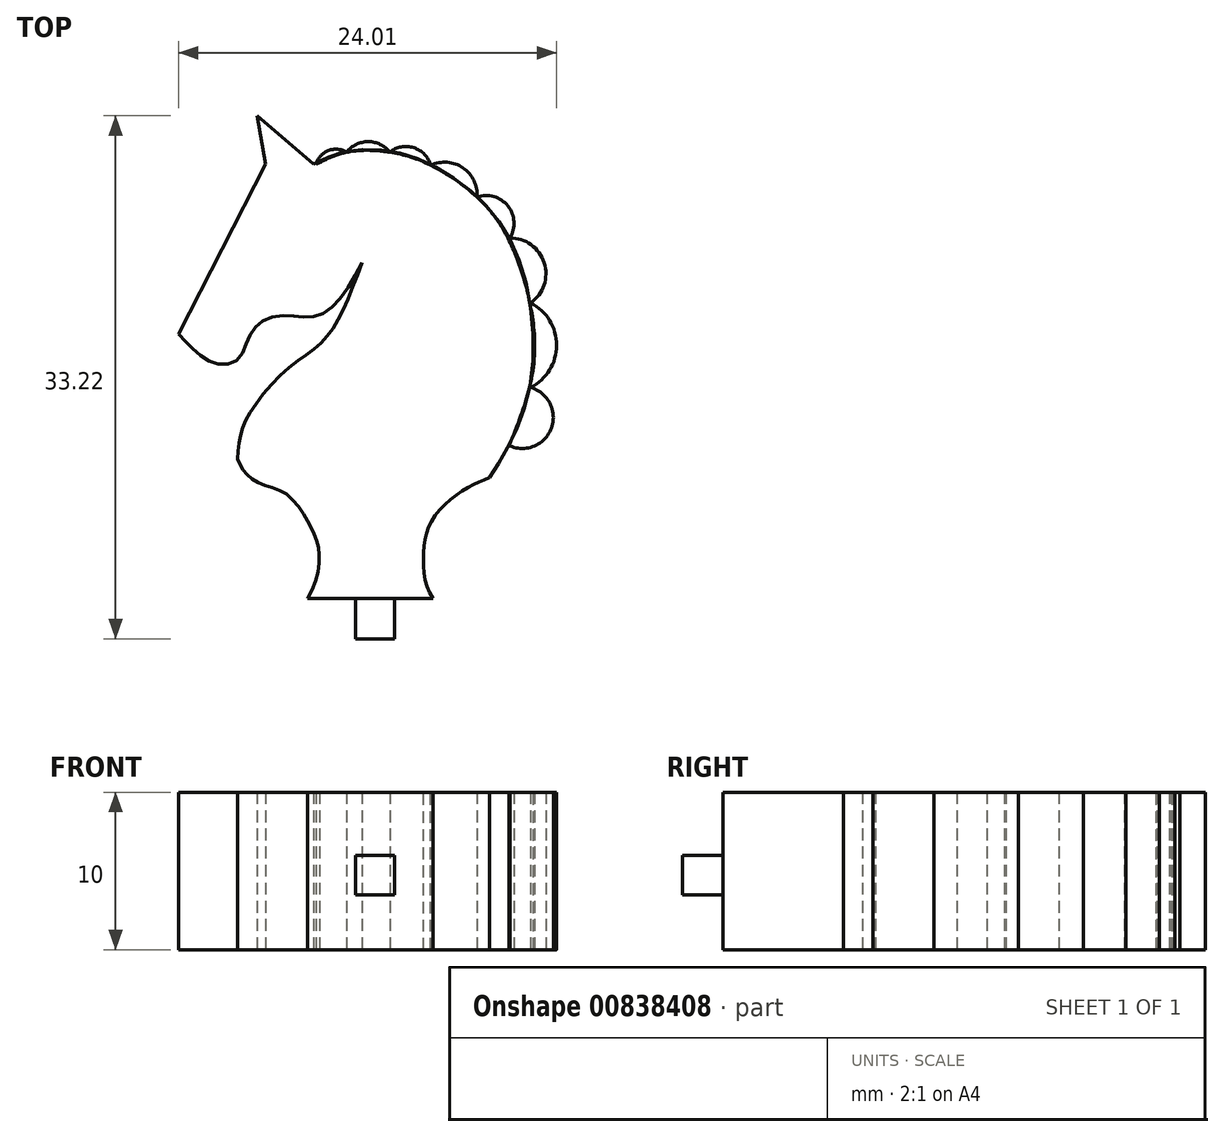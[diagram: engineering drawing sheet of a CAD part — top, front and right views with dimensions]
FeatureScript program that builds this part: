
annotation { "Feature Type Name" : "Feature", "Feature Type Description" : "" }
export const myFeature = defineFeature(function(context is Context, id is Id, definition is map)
    precondition{}
    {
        {
            var Q0;
            Q0=qCreatedBy(makeId("Top.planeOp"),FACE);
            var sketch = newSketch(context, id + "F0", { "sketchPlane" : qUnion([Q0])});
            skLineSegment(sketch, "E0", {"start": v(-12.48, 16.9) * mm, "end": v(-6.96, 27.69) * mm});
            skLineSegment(sketch, "E1", {"start": v(-6.96, 27.69) * mm, "end": v(-7.5, 30.77) * mm});
            skLineSegment(sketch, "E2", {"start": v(-7.5, 30.77) * mm, "end": v(-3.91, 27.69) * mm});
            skFitSpline(sketch, "E3", {"points": [v(-3.91, 27.69) * mm, v(-1.87, 28.5) * mm, v(0.86, 28.54) * mm, v(3.5, 27.69) * mm, v(6.44, 25.66) * mm, v(8.5, 23.04) * mm, v(9.85, 18.85) * mm, v(9.81, 13.52) * mm, v(8.53, 9.9) * mm, v(7.26, 7.78) * mm], "startDerivative": vector(21.4, 10.83) * mm, "endDerivative": vector(-13.49, -20.71) * mm});
            skFitSpline(sketch, "E4", {"points": [v(7.26, 7.78) * mm, v(5.6, 7) * mm, v(3.66, 5.15) * mm, v(3.09, 3.13) * mm, v(3.34, 0.79) * mm, v(4.65, -1.02) * mm, v(6.14, -1.95) * mm, v(7.6, -2.36) * mm], "startDerivative": vector(-11.83, -4.62) * mm, "endDerivative": vector(12.03, -2.67) * mm});
            skFitSpline(sketch, "E5", {"points": [v(-12.48, 16.9) * mm, v(-11.34, 15.75) * mm, v(-10, 15) * mm, v(-8.68, 15.33) * mm, v(-8.05, 16.63) * mm, v(-7.17, 17.71) * mm, v(-5.51, 18.09) * mm, v(-3.91, 18.01) * mm, v(-2.43, 18.92) * mm, v(-0.82, 21.45) * mm], "startDerivative": vector(10.15, -10.82) * mm, "endDerivative": vector(10.23, 19.07) * mm});
            skFitSpline(sketch, "E6", {"points": [v(-0.82, 21.45) * mm, v(-2.27, 17.96) * mm, v(-3.6, 16.18) * mm, v(-5.61, 14.65) * mm, v(-7.9, 11.99) * mm, v(-8.55, 10.48) * mm, v(-8.73, 8.97) * mm], "startDerivative": vector(-6.89, -18.3) * mm, "endDerivative": vector(-0.81, -11.84) * mm});
            skFitSpline(sketch, "E7", {"points": [v(-8.73, 8.97) * mm, v(-8.23, 8.08) * mm, v(-7.19, 7.37) * mm, v(-5.68, 6.77) * mm, v(-4.38, 5.2) * mm, v(-3.75, 3.89) * mm, v(-3.54, 2.38) * mm, v(-4.28, 0.1) * mm, v(-5.52, -1.32) * mm, v(-6.69, -2.04) * mm, v(-8.3, -2.4) * mm], "startDerivative": vector(5.04, -11.7) * mm, "endDerivative": vector(-16.8, -2.54) * mm});
            skLineSegment(sketch, "E8", {"start": v(-4.28, 0.1) * mm, "end": v(3.68, 0.1) * mm});
            skLineSegment(sketch, "E9", {"start": v(3.68, 0.1) * mm, "end": v(1.16, 0.1) * mm});
            skLineSegment(sketch, "E10", {"start": v(-4.28, 0.1) * mm, "end": v(-1.8, 0.1) * mm});
            skPoint(sketch, "E11.end.orphan", {"position": v(1.16, -4.9) * mm});
            skPoint(sketch, "E11.start.orphan", {"position": v(-1.8, -4.9) * mm});
            skSolve(sketch);
        }
        {
            var Q0;
            Q0=qCreatedBy(makeId("Top.planeOp"),FACE);
            var sketch = newSketch(context, id + "F1", { "sketchPlane" : qUnion([Q0])});
            skArc(sketch, "E12", {"start": v(-1.8, 28.46) * mm, "mid": v(-2.98, 28.56) * mm, "end": v(-3.76, 27.68) * mm});
            skArc(sketch, "E13", {"start": v(0.94, 28.46) * mm, "mid": v(-0.43, 29.13) * mm, "end": v(-1.8, 28.46) * mm});
            skArc(sketch, "E14", {"start": v(3.53, 27.63) * mm, "mid": v(2.46, 28.74) * mm, "end": v(0.94, 28.46) * mm});
            skArc(sketch, "E15", {"start": v(6.48, 25.6) * mm, "mid": v(5.59, 27.46) * mm, "end": v(3.53, 27.63) * mm});
            skArc(sketch, "E16", {"start": v(8.56, 23.01) * mm, "mid": v(8.44, 25.05) * mm, "end": v(6.48, 25.6) * mm});
            skArc(sketch, "E17", {"start": v(9.89, 18.88) * mm, "mid": v(10.74, 21.44) * mm, "end": v(8.56, 23.01) * mm});
            skArc(sketch, "E18", {"start": v(9.89, 13.51) * mm, "mid": v(11.53, 16.2) * mm, "end": v(9.89, 18.88) * mm});
            skArc(sketch, "E19", {"start": v(8.56, 9.8) * mm, "mid": v(11.2, 10.94) * mm, "end": v(9.89, 13.51) * mm});
            skLineSegment(sketch, "E20", {"start": v(9.89, 13.51) * mm, "end": v(9.81, 13.53) * mm});
            skLineSegment(sketch, "E21", {"start": v(9.89, 18.88) * mm, "end": v(9.83, 18.88) * mm});
            skLineSegment(sketch, "E22", {"start": v(8.56, 23.01) * mm, "end": v(8.43, 23.01) * mm});
            skLineSegment(sketch, "E23", {"start": v(-1.8, 28.46) * mm, "end": v(-1.8, 28.46) * mm});
            skFitSpline(sketch, "E24", {"points": [v(-3.76, 27.68) * mm, v(-1.8, 28.46) * mm, v(0.94, 28.46) * mm, v(3.53, 27.63) * mm, v(6.48, 25.6) * mm, v(8.43, 23.01) * mm, v(9.83, 18.88) * mm, v(9.81, 13.53) * mm, v(8.5, 9.8) * mm, v(8.5, 9.8) * mm], "startDerivative": vector(18.81, 9.57) * mm, "endDerivative": vector(0.25, 0.1) * mm});
            skLineSegment(sketch, "E25", {"start": v(8.56, 9.8) * mm, "end": v(8.5, 9.8) * mm});
            skSolve(sketch);
        }
        {
            var Q0;
            Q0=makeQuery(id+"F1.imprint","IMPRINT",FACE,{"disambiguationData":[TD([[makeQuery(id+"F1.imprint","IMPRINT",EDGE,{"derivedFrom":sQuery(id+"F1.wireOp",EDGE,"E17")}),1.0]])]});
            var Q1;
            Q1=makeQuery(id+"F1.imprint","IMPRINT",FACE,{"disambiguationData":[TD([[makeQuery(id+"F1.imprint","IMPRINT",EDGE,{"derivedFrom":sQuery(id+"F1.wireOp",EDGE,"E18")}),1.0]])]});
            var Q2;
            Q2=makeQuery(id+"F1.imprint","IMPRINT",FACE,{"disambiguationData":[TD([[makeQuery(id+"F1.imprint","IMPRINT",EDGE,{"derivedFrom":sQuery(id+"F1.wireOp",EDGE,"E19")}),1.0]])]});
            var Q3;
            {var subQ0=sQuery(id+"F1.wireOp",EDGE,"E16");Q3=makeQuery(id+"F1.imprint","IMPRINT",FACE,{"disambiguationData":[TD([[makeQuery(id+"F1.imprint","IMPRINT",EDGE,{"derivedFrom":subQ0}),1.0]])]});}
            var Q4;
            {var subQ0=sQuery(id+"F1.wireOp",EDGE,"E15");Q4=makeQuery(id+"F1.imprint","IMPRINT",FACE,{"disambiguationData":[TD([[makeQuery(id+"F1.imprint","IMPRINT",EDGE,{"derivedFrom":subQ0}),1.0]])]});}
            var Q5;
            {var subQ0=sQuery(id+"F1.wireOp",EDGE,"E14");Q5=makeQuery(id+"F1.imprint","IMPRINT",FACE,{"disambiguationData":[TD([[makeQuery(id+"F1.imprint","IMPRINT",EDGE,{"derivedFrom":subQ0}),1.0]])]});}
            var Q6;
            {var subQ0=sQuery(id+"F1.wireOp",EDGE,"E13");Q6=makeQuery(id+"F1.imprint","IMPRINT",FACE,{"disambiguationData":[TD([[makeQuery(id+"F1.imprint","IMPRINT",EDGE,{"derivedFrom":subQ0}),1.0]])]});}
            var Q7;
            {var subQ0=sQuery(id+"F1.wireOp",EDGE,"E12");Q7=makeQuery(id+"F1.imprint","IMPRINT",FACE,{"disambiguationData":[TD([[makeQuery(id+"F1.imprint","IMPRINT",EDGE,{"derivedFrom":subQ0}),1.0]])]});}
            extrude(context, id + "F2", {"entities" : qUnion([Q0, Q1, Q2, Q3, Q4, Q5, Q6, Q7]), "depth" : 10 * mm, "offsetDistance" : 25 * mm});
        }
        {
            var Q0;
            Q0=makeQuery(id+"F0.imprint","IMPRINT",FACE,{"disambiguationData":[TD([[makeQuery(id+"F0.imprint","IMPRINT",EDGE,{"derivedFrom":sQuery(id+"F0.wireOp",EDGE,"E0")}),-1.0]])]});
            extrude(context, id + "F3", {"entities" : qUnion([Q0]), "depth" : 10 * mm, "offsetDistance" : 25 * mm});
        }
        {
            var Q0;
            Q0=makeQuery(id+"F3.opExtrude","SWEPT_FACE",FACE,{"disambiguationData":[OSD([sQuery(id+"F0.wireOp",EDGE,"E8"),sQuery(id+"F0.wireOp",EDGE,"E9"),sQuery(id+"F0.wireOp",EDGE,"E10")])]});
            var sketch = newSketch(context, id + "F4", { "sketchPlane" : qUnion([Q0])});
            skSolve(sketch);
        }
        {
            var Q0;
            {var subQ1=sQuery(id+"F0.wireOp",EDGE,"E9");var subQ4=makeQuery(id+"F3.opExtrude","SWEPT_EDGE",EDGE,{"disambiguationData":[OSD([sQuery(id+"F0.wireOp",EDGE,"E4"),subQ1])]});Q0=makeQuery(id+"F4.imprint","IMPRINT",FACE,{"disambiguationData":[TD([[makeQuery(id+"F4.imprint","IMPRINT",EDGE,{"derivedFrom":subQ4}),-1.0]])]});}
            var sketch = newSketch(context, id + "F5", { "sketchPlane" : qUnion([Q0])});
            skLineSegment(sketch, "E26.bottom", {"start": v(1.25, 6) * mm, "end": v(-1.25, 6) * mm});
            skLineSegment(sketch, "E26.top", {"start": v(1.25, 3.5) * mm, "end": v(-1.25, 3.5) * mm});
            skLineSegment(sketch, "E26.left", {"start": v(1.25, 6) * mm, "end": v(1.25, 3.5) * mm});
            skLineSegment(sketch, "E26.right", {"start": v(-1.25, 6) * mm, "end": v(-1.25, 3.5) * mm});
            skPoint(sketch, "E26.middle", {"position": v(0, 4.75) * mm});
            skSolve(sketch);
        }
        {
            var Q0;
            Q0=makeQuery(id+"F5.imprint","IMPRINT",FACE,{"disambiguationData":[TD([[makeQuery(id+"F5.imprint","IMPRINT",EDGE,{"derivedFrom":sQuery(id+"F5.wireOp",EDGE,"E26.bottom")}),1.0]])]});
            extrude(context, id + "F6", {"entities" : qUnion([Q0]), "operationType" : NewBodyOperationType.ADD, "depth" : 2.55 * mm, "offsetDistance" : 25 * mm});
        }
    });
